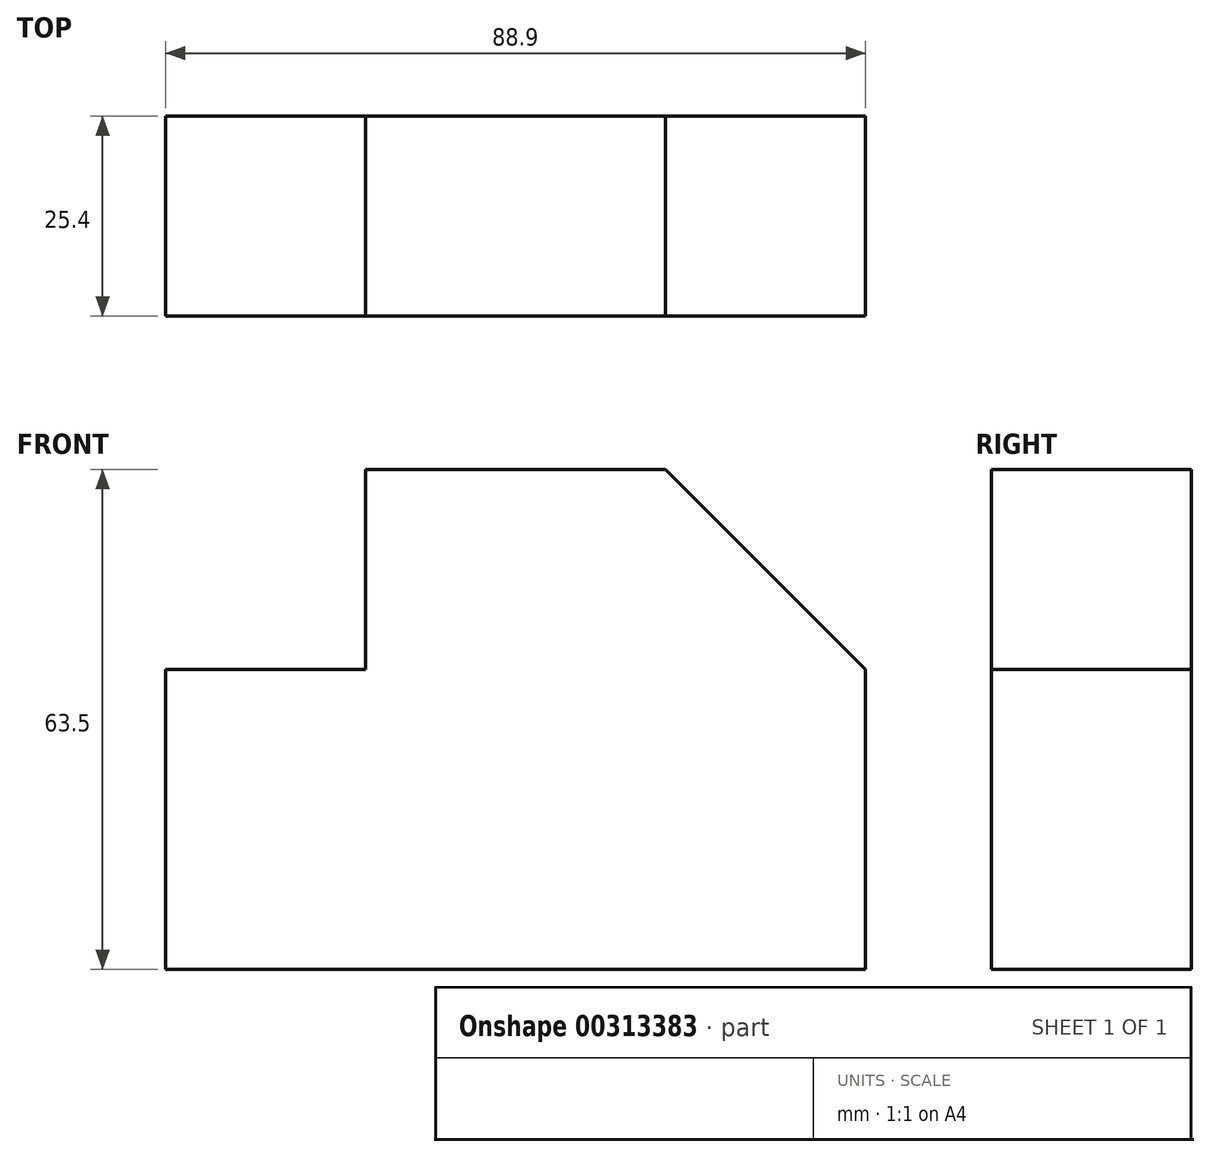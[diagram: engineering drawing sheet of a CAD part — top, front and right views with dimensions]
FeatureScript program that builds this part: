
annotation { "Feature Type Name" : "Feature", "Feature Type Description" : "" }
export const myFeature = defineFeature(function(context is Context, id is Id, definition is map)
    precondition{}
    {
        {
            var Q0;
            Q0=qCreatedBy(makeId("Front.planeOp"),FACE);
            var sketch = newSketch(context, id + "F0", { "sketchPlane" : qUnion([Q0])});
            skLineSegment(sketch, "E0", {"start": v(-40.35, -20) * mm, "end": v(48.55, -20) * mm});
            skLineSegment(sketch, "E1", {"start": v(48.55, -20) * mm, "end": v(48.55, 18.1) * mm});
            skLineSegment(sketch, "E2", {"start": v(-40.35, -20) * mm, "end": v(-40.35, 18.1) * mm});
            skLineSegment(sketch, "E3", {"start": v(-40.35, 18.1) * mm, "end": v(-14.95, 18.1) * mm});
            skLineSegment(sketch, "E4", {"start": v(-14.95, 18.1) * mm, "end": v(-14.95, 43.5) * mm});
            skLineSegment(sketch, "E5", {"start": v(-14.95, 43.5) * mm, "end": v(23.15, 43.5) * mm});
            skLineSegment(sketch, "E6", {"start": v(23.15, 43.5) * mm, "end": v(48.55, 18.1) * mm});
            skSolve(sketch);
        }
        {
            var Q0;
            Q0 = qSketchRegion(id + "F0", true);
            extrude(context, id + "F1", {"entities" : qUnion([Q0]), "depth" : 25.4 * mm});
        }
    });
